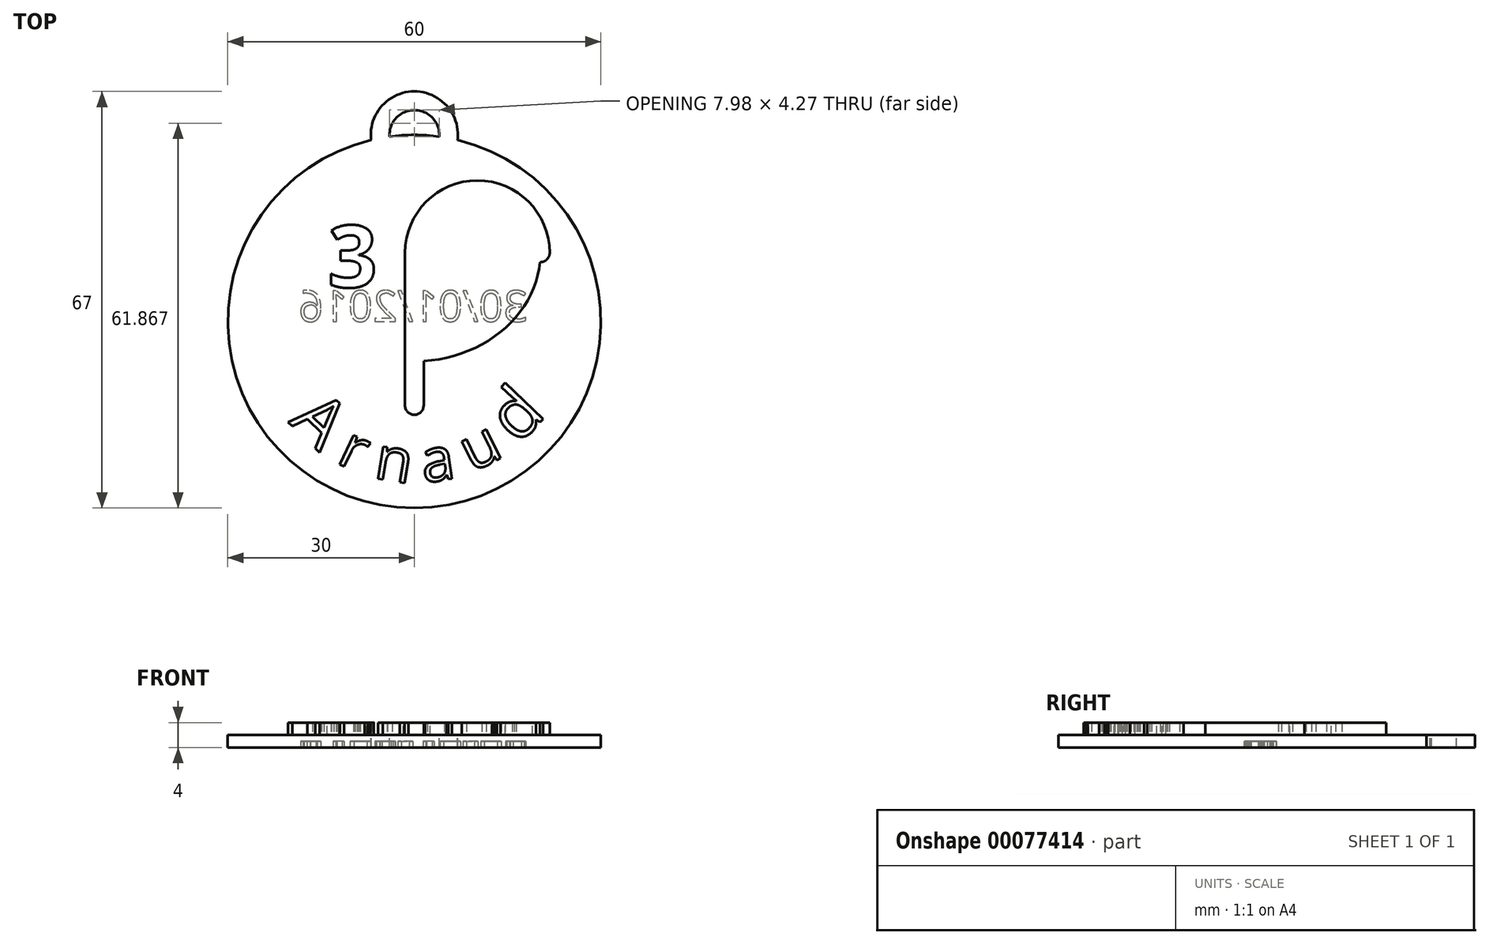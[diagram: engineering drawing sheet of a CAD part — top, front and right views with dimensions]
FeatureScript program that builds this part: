
annotation { "Feature Type Name" : "Feature", "Feature Type Description" : "" }
export const myFeature = defineFeature(function(context is Context, id is Id, definition is map)
    precondition{}
    {
        {
            var Q0;
            Q0=qCreatedBy(makeId("Top.planeOp"),FACE);
            var sketch = newSketch(context, id + "F0", { "sketchPlane" : qUnion([Q0])});
            skCircle(sketch, "E0", {"center": v(0, 0) * mm, "radius": 30 * mm});
            skSolve(sketch);
        }
        {
            var Q0;
            Q0=qSketchRegion(id+"F0",true);
            extrude(context, id + "F1", {"entities" : qUnion([Q0]), "oppositeDirection" : true, "depth" : 2 * mm});
        }
        {
            var Q0;
            Q0=qCreatedBy(makeId("Top.planeOp"),FACE);
            var sketch = newSketch(context, id + "F2", { "sketchPlane" : qUnion([Q0])});
            skEllipticalArc(sketch, "E1", {});
            skLineSegment(sketch, "E2", {"start": v(0, 0) * mm, "end": v(0, 30) * mm, "construction": true});
            skLineSegment(sketch, "E3", {"start": v(0, 11.04) * mm, "end": v(0, -13.5) * mm});
            skArc(sketch, "E4", {"start": v(20.27, 11.04) * mm, "mid": v(10.13, 21.17) * mm, "end": v(0, 11.04) * mm});
            skLineSegment(sketch, "E5", {"start": v(0, 11.04) * mm, "end": v(-16.84, 20.76) * mm, "construction": true});
            skLineSegment(sketch, "E6", {"start": v(0, 11.04) * mm, "end": v(-20.27, 11.04) * mm, "construction": true});
            skArc(sketch, "E7.0.startCap", {"start": v(-1.5, 11.04) * mm, "mid": v(0, 12.54) * mm, "end": v(1.5, 11.04) * mm});
            skArc(sketch, "E7.0.endCap", {"start": v(1.5, -13.5) * mm, "mid": v(0, -15) * mm, "end": v(-1.5, -13.5) * mm});
            skLineSegment(sketch, "E7.0.left", {"start": v(1.5, 11.04) * mm, "end": v(1.5, -13.5) * mm});
            skLineSegment(sketch, "E7.0.right", {"start": v(-1.5, 11.04) * mm, "end": v(-1.5, -13.5) * mm});
            skArc(sketch, "E8.0.startCap", {"start": v(21.77, 11.04) * mm, "mid": v(20.27, 9.54) * mm, "end": v(18.77, 11.04) * mm});
            skArc(sketch, "E8.0.endCap", {"start": v(1.5, 11.04) * mm, "mid": v(0, 9.54) * mm, "end": v(-1.5, 11.04) * mm});
            skArc(sketch, "E8.0.left", {"start": v(18.77, 11.04) * mm, "mid": v(10.13, 19.67) * mm, "end": v(1.5, 11.04) * mm});
            skArc(sketch, "E8.0.right", {"start": v(21.77, 11.04) * mm, "mid": v(10.13, 22.67) * mm, "end": v(-1.5, 11.04) * mm});
            skArc(sketch, "E8.1.startCap", {"start": v(-18.02, 21.68) * mm, "mid": v(-15.91, 21.95) * mm, "end": v(-15.65, 19.84) * mm});
            skArc(sketch, "E8.1.endCap", {"start": v(18.77, 11.04) * mm, "mid": v(20.27, 12.54) * mm, "end": v(21.77, 11.04) * mm});
            skFitSpline(sketch, "E8.1.left", {"points": [v(18.7, 9.5) * mm, v(18.8, 11.04) * mm, v(18.7, 12.6) * mm, v(18.36, 14.63) * mm, v(17.66, 16.6) * mm, v(16.63, 18.49) * mm, v(15.37, 20.3) * mm, v(13.44, 22.32) * mm, v(11.07, 24) * mm, v(8.94, 25.1) * mm, v(6.7, 26.01) * mm, v(4.32, 26.63) * mm, v(1.87, 26.95) * mm, v(0, 27.03) * mm, v(-1.87, 26.95) * mm, v(-4.32, 26.63) * mm, v(-6.7, 26.01) * mm, v(-8.94, 25.1) * mm, v(-11.07, 24) * mm, v(-13.44, 22.32) * mm, v(-15.37, 20.3) * mm, v(-16.63, 18.49) * mm, v(-17.66, 16.6) * mm, v(-18.36, 14.63) * mm, v(-18.7, 12.6) * mm, v(-18.8, 11.04) * mm, v(-18.7, 9.5) * mm, v(-18.36, 7.46) * mm, v(-17.66, 5.48) * mm, v(-16.63, 3.6) * mm, v(-15.37, 1.8) * mm, v(-13.44, -0.24) * mm, v(-11.07, -1.92) * mm, v(-8.94, -3.02) * mm, v(-6.7, -3.93) * mm, v(-4.32, -4.55) * mm, v(-1.87, -4.86) * mm, v(0, -4.94) * mm, v(1.87, -4.86) * mm, v(4.32, -4.55) * mm, v(6.7, -3.93) * mm, v(8.94, -3.02) * mm, v(11.07, -1.92) * mm, v(13.44, -0.24) * mm, v(15.37, 1.8) * mm, v(16.63, 3.6) * mm, v(17.66, 5.48) * mm, v(18.36, 7.46) * mm, v(18.7, 9.5) * mm, v(18.8, 11.04) * mm, v(18.7, 12.6) * mm]});
            skFitSpline(sketch, "E8.1.right", {"points": [v(21.7, 9.15) * mm, v(21.8, 11.04) * mm, v(21.7, 12.93) * mm, v(21.27, 15.42) * mm, v(20.42, 17.81) * mm, v(19.18, 20.07) * mm, v(17.69, 22.22) * mm, v(15.4, 24.61) * mm, v(12.65, 26.56) * mm, v(10.2, 27.83) * mm, v(7.62, 28.88) * mm, v(4.92, 29.58) * mm, v(2.12, 29.94) * mm, v(0, 30.03) * mm, v(-2.12, 29.94) * mm, v(-4.92, 29.58) * mm, v(-7.62, 28.88) * mm, v(-10.2, 27.83) * mm, v(-12.65, 26.56) * mm, v(-15.4, 24.61) * mm, v(-17.69, 22.22) * mm, v(-19.18, 20.07) * mm, v(-20.42, 17.81) * mm, v(-21.27, 15.42) * mm, v(-21.7, 12.93) * mm, v(-21.8, 11.04) * mm, v(-21.7, 9.15) * mm, v(-21.27, 6.67) * mm, v(-20.42, 4.27) * mm, v(-19.18, 2) * mm, v(-17.69, -0.14) * mm, v(-15.4, -2.53) * mm, v(-12.65, -4.48) * mm, v(-10.2, -5.75) * mm, v(-7.62, -6.8) * mm, v(-4.92, -7.5) * mm, v(-2.12, -7.86) * mm, v(0, -7.95) * mm, v(2.12, -7.86) * mm, v(4.92, -7.5) * mm, v(7.62, -6.8) * mm, v(10.2, -5.75) * mm, v(12.65, -4.48) * mm, v(15.4, -2.53) * mm, v(17.69, -0.14) * mm, v(19.18, 2) * mm, v(20.42, 4.27) * mm, v(21.27, 6.67) * mm, v(21.7, 9.15) * mm, v(21.8, 11.04) * mm, v(21.7, 12.93) * mm]});
            const initialGuessF2  = {"E1": [0, 0.011041626236194823, 1, 0, 0.020266667008310185, 0.017458373763805178, 2.5511335140588507, 0]};
            skSetInitialGuess(sketch, initialGuessF2);
            skSolve(sketch);
        }
        {
            var Q0;
            {var subQ0=sQuery(id+"F2.wireOp",EDGE,"E8.1.startCap");Q0=makeQuery(id+"F2.imprint","IMPRINT",FACE,{"disambiguationData":[TD([[makeQuery(id+"F2.imprint","IMPRINT",EDGE,{"derivedFrom":subQ0}),-1.0]])]});}
            var Q1;
            {var subQ0=sQuery(id+"F2.wireOp",EDGE,"E7.0.right");var subQ1=sQuery(id+"F2.wireOp",EDGE,"E1");var subQ2=makeQuery(id+"F2.imprint","INTERSECT",VERTEX,{"derivedFrom":[subQ1,subQ0]});Q1=makeQuery(id+"F2.imprint","IMPRINT",FACE,{"disambiguationData":[TD([[makeQuery(id+"F2.imprint","IMPRINT",EDGE,{"disambiguationData":[TD([[subQ2,-1.0]])],"derivedFrom":subQ1}),1.0]])]});}
            var Q2;
            {var subQ0=sQuery(id+"F2.wireOp",EDGE,"E3");var subQ1=sQuery(id+"F2.wireOp",EDGE,"E1");var subQ2=makeQuery(id+"F2.imprint","INTERSECT",VERTEX,{"derivedFrom":[subQ1,subQ0]});Q2=makeQuery(id+"F2.imprint","IMPRINT",FACE,{"disambiguationData":[TD([[makeQuery(id+"F2.imprint","IMPRINT",EDGE,{"disambiguationData":[TD([[subQ2,-1.0]])],"derivedFrom":subQ1}),1.0]])]});}
            var Q3;
            {var subQ0=sQuery(id+"F2.wireOp",EDGE,"E7.0.right");var subQ1=sQuery(id+"F2.wireOp",EDGE,"E1");var subQ2=makeQuery(id+"F2.imprint","INTERSECT",VERTEX,{"derivedFrom":[subQ1,subQ0]});Q3=makeQuery(id+"F2.imprint","IMPRINT",FACE,{"disambiguationData":[TD([[makeQuery(id+"F2.imprint","IMPRINT",EDGE,{"disambiguationData":[TD([[subQ2,-1.0]])],"derivedFrom":subQ1}),-1.0]])]});}
            var Q4;
            {var subQ0=sQuery(id+"F2.wireOp",EDGE,"E3");var subQ1=sQuery(id+"F2.wireOp",EDGE,"E1");var subQ2=makeQuery(id+"F2.imprint","INTERSECT",VERTEX,{"derivedFrom":[subQ1,subQ0]});Q4=makeQuery(id+"F2.imprint","IMPRINT",FACE,{"disambiguationData":[TD([[makeQuery(id+"F2.imprint","IMPRINT",EDGE,{"disambiguationData":[TD([[subQ2,-1.0]])],"derivedFrom":subQ1}),-1.0]])]});}
            var Q5;
            {var subQ0=sQuery(id+"F2.wireOp",EDGE,"E7.0.left");var subQ1=sQuery(id+"F2.wireOp",EDGE,"E1");var subQ2=makeQuery(id+"F2.imprint","INTERSECT",VERTEX,{"derivedFrom":[subQ1,subQ0]});Q5=makeQuery(id+"F2.imprint","IMPRINT",FACE,{"disambiguationData":[TD([[makeQuery(id+"F2.imprint","IMPRINT",EDGE,{"disambiguationData":[TD([[subQ2,-1.0]])],"derivedFrom":subQ1}),-1.0]])]});}
            var Q6;
            {var subQ0=sQuery(id+"F2.wireOp",EDGE,"E7.0.left");var subQ1=sQuery(id+"F2.wireOp",EDGE,"E1");var subQ2=makeQuery(id+"F2.imprint","INTERSECT",VERTEX,{"derivedFrom":[subQ1,subQ0]});Q6=makeQuery(id+"F2.imprint","IMPRINT",FACE,{"disambiguationData":[TD([[makeQuery(id+"F2.imprint","IMPRINT",EDGE,{"disambiguationData":[TD([[subQ2,-1.0]])],"derivedFrom":subQ1}),1.0]])]});}
            var Q7;
            {var subQ0=sQuery(id+"F2.wireOp",EDGE,"E4");var subQ1=sQuery(id+"F2.wireOp",EDGE,"E1");var subQ2=makeQuery(id+"F2.imprint","INTERSECT",VERTEX,{"derivedFrom":[subQ1,subQ0]});Q7=makeQuery(id+"F2.imprint","IMPRINT",FACE,{"disambiguationData":[TD([[makeQuery(id+"F2.imprint","IMPRINT",EDGE,{"disambiguationData":[TD([[subQ2,1.0]])],"derivedFrom":subQ1}),-1.0]])]});}
            var Q8;
            {var subQ0=sQuery(id+"F2.wireOp",EDGE,"E4");var subQ1=sQuery(id+"F2.wireOp",EDGE,"E1");var subQ2=makeQuery(id+"F2.imprint","INTERSECT",VERTEX,{"derivedFrom":[subQ1,subQ0]});Q8=makeQuery(id+"F2.imprint","IMPRINT",FACE,{"disambiguationData":[TD([[makeQuery(id+"F2.imprint","IMPRINT",EDGE,{"disambiguationData":[TD([[subQ2,1.0]])],"derivedFrom":subQ1}),1.0]])]});}
            var Q9;
            {var subQ5=sQuery(id+"F2.wireOp",EDGE,"E8.0.left");Q9=makeQuery(id+"F2.imprint","IMPRINT",FACE,{"disambiguationData":[TD([[makeQuery(id+"F2.imprint","IMPRINT",EDGE,{"derivedFrom":subQ5}),-1.0]])]});}
            var Q10;
            {var subQ5=sQuery(id+"F2.wireOp",EDGE,"E8.0.right");Q10=makeQuery(id+"F2.imprint","IMPRINT",FACE,{"disambiguationData":[TD([[makeQuery(id+"F2.imprint","IMPRINT",EDGE,{"derivedFrom":subQ5}),1.0]])]});}
            var Q11;
            {var subQ0=sQuery(id+"F2.wireOp",EDGE,"E4");var subQ1=sQuery(id+"F2.wireOp",EDGE,"E3");var subQ2=makeQuery(id+"F2.imprint","INTERSECT",VERTEX,{"derivedFrom":[subQ1,subQ0]});Q11=makeQuery(id+"F2.imprint","IMPRINT",FACE,{"disambiguationData":[TD([[makeQuery(id+"F2.imprint","IMPRINT",EDGE,{"disambiguationData":[TD([[subQ2,-1.0]])],"derivedFrom":subQ1}),-1.0]])]});}
            var Q12;
            {var subQ0=sQuery(id+"F2.wireOp",EDGE,"E4");var subQ1=sQuery(id+"F2.wireOp",EDGE,"E3");var subQ2=makeQuery(id+"F2.imprint","INTERSECT",VERTEX,{"derivedFrom":[subQ1,subQ0]});Q12=makeQuery(id+"F2.imprint","IMPRINT",FACE,{"disambiguationData":[TD([[makeQuery(id+"F2.imprint","IMPRINT",EDGE,{"disambiguationData":[TD([[subQ2,-1.0]])],"derivedFrom":subQ1}),1.0]])]});}
            var Q13;
            {var subQ0=sQuery(id+"F2.wireOp",EDGE,"E8.0.endCap");var subQ1=sQuery(id+"F2.wireOp",EDGE,"E3");var subQ2=makeQuery(id+"F2.imprint","INTERSECT",VERTEX,{"derivedFrom":[subQ1,subQ0]});Q13=makeQuery(id+"F2.imprint","IMPRINT",FACE,{"disambiguationData":[TD([[makeQuery(id+"F2.imprint","IMPRINT",EDGE,{"disambiguationData":[TD([[subQ2,-1.0]])],"derivedFrom":subQ1}),-1.0]])]});}
            var Q14;
            {var subQ0=sQuery(id+"F2.wireOp",EDGE,"E8.0.endCap");var subQ1=sQuery(id+"F2.wireOp",EDGE,"E3");var subQ2=makeQuery(id+"F2.imprint","INTERSECT",VERTEX,{"derivedFrom":[subQ1,subQ0]});Q14=makeQuery(id+"F2.imprint","IMPRINT",FACE,{"disambiguationData":[TD([[makeQuery(id+"F2.imprint","IMPRINT",EDGE,{"disambiguationData":[TD([[subQ2,-1.0]])],"derivedFrom":subQ1}),1.0]])]});}
            var Q15;
            {var subQ1=sQuery(id+"F2.wireOp",EDGE,"E7.0.endCap");Q15=makeQuery(id+"F2.imprint","IMPRINT",FACE,{"disambiguationData":[TD([[makeQuery(id+"F2.imprint","IMPRINT",EDGE,{"derivedFrom":subQ1}),-1.0]])]});}
            extrude(context, id + "F3", {"entities" : qUnion([Q0, Q1, Q2, Q3, Q4, Q5, Q6, Q7, Q8, Q9, Q10, Q11, Q12, Q13, Q14, Q15]), "operationType" : NewBodyOperationType.ADD, "depth" : 2 * mm});
        }
        {
            var Q0;
            Q0=qCreatedBy(makeId("Top.planeOp"),FACE);
            var sketch = newSketch(context, id + "F4", { "sketchPlane" : qUnion([Q0])});
            skText(sketch, "E9", { "text": "3", "fontName": "OpenSans-Bold.ttf"});
            skText(sketch, "E10", { "text": "D", "fontName": "OpenSans-Bold.ttf"});
            const initialGuessF4  = {"E9": [-0.0139, 0.0055, 1, 0, 0.01], "E10": [0.0055, 0.0055, 1, 0, 0.01]};
            skSetInitialGuess(sketch, initialGuessF4);
            skSolve(sketch);
        }
        {
            var Q0;
            Q0=qSketchRegion(id+"F4",true);
            extrude(context, id + "F5", {"entities" : qUnion([Q0]), "operationType" : NewBodyOperationType.ADD, "depth" : 2 * mm});
        }
        {
            var Q0;
            {var subQ8=sQuery(id+"F0.wireOp",EDGE,"E0");Q0=makeQuery(id+"F3.boolean.opBoolean","SPLIT",FACE,{"disambiguationData":[TD([makeQuery(id+"F1.opExtrude","SWEPT_FACE",FACE,{"disambiguationData":[OSD([subQ8])]})])],"derivedFrom":makeQuery(id+"F1.opExtrude","CAP_FACE",FACE,{"disambiguationData":[OSD([subQ8])],"isStart":true})});}
            var sketch = newSketch(context, id + "F6", { "sketchPlane" : qUnion([Q0])});
            skCircle(sketch, "E11.0", {"center": v(0, 0) * mm, "radius": 26 * mm, "construction": true});
            skText(sketch, "E12", { "text": "A", "fontName": "OpenSans-Regular.ttf"});
            skText(sketch, "E13", { "text": "r", "fontName": "OpenSans-Regular.ttf"});
            skText(sketch, "E14", { "text": "n", "fontName": "OpenSans-Regular.ttf"});
            skText(sketch, "E15", { "text": "a", "fontName": "OpenSans-Regular.ttf"});
            skText(sketch, "E16", { "text": "u", "fontName": "OpenSans-Regular.ttf"});
            skText(sketch, "E17", { "text": "d", "fontName": "OpenSans-Regular.ttf"});
            const initialGuessF6  = {"E12": [-0.02032, -0.01622, 0.72378, -0.69003, 0.008], "E13": [-0.01277, -0.02265, 0.90486, -0.42571, 0.007], "E14": [-0.00667, -0.02513, 0.98728, -0.15902, 0.007], "E15": [0.00149, -0.02596, 0.98934, 0.1456, 0.007], "E16": [0.00928, -0.02429, 0.8943, 0.44747, 0.007], "E17": [0.0167, -0.01993, 0.68945, 0.72433, 0.008]};
            skSetInitialGuess(sketch, initialGuessF6);
            skSolve(sketch);
        }
        {
            var Q0;
            Q0=qSketchRegion(id+"F6",true);
            extrude(context, id + "F7", {"entities" : qUnion([Q0]), "operationType" : NewBodyOperationType.ADD, "depth" : 2 * mm});
        }
        {
            var Q0;
            Q0=qCreatedBy(makeId("Top.planeOp"),FACE);
            var sketch = newSketch(context, id + "F8", { "sketchPlane" : qUnion([Q0])});
            skArc(sketch, "E18", {"start": v(5.48, 29.5) * mm, "mid": v(0, 35.5) * mm, "end": v(-5.48, 29.5) * mm});
            skArc(sketch, "E19.0.startCap", {"start": v(6.97, 29.36) * mm, "mid": v(5.34, 28) * mm, "end": v(3.98, 29.63) * mm});
            skArc(sketch, "E19.0.endCap", {"start": v(-3.98, 29.63) * mm, "mid": v(-5.34, 28) * mm, "end": v(-6.97, 29.36) * mm});
            skArc(sketch, "E19.0.left", {"start": v(3.98, 29.63) * mm, "mid": v(0, 34) * mm, "end": v(-3.98, 29.63) * mm});
            skArc(sketch, "E19.0.right", {"start": v(6.97, 29.36) * mm, "mid": v(0, 37) * mm, "end": v(-6.97, 29.36) * mm});
            skSolve(sketch);
        }
        {
            var Q0;
            Q0=qSketchRegion(id+"F8",true);
            extrude(context, id + "F9", {"entities" : qUnion([Q0]), "operationType" : NewBodyOperationType.ADD, "oppositeDirection" : true, "depth" : 2 * mm});
        }
        {
            var Q0;
            Q0=makeQuery(id+"F9.boolean.opBoolean","MERGE",FACE,{"derivedFrom":[makeQuery(id+"F1.opExtrude","CAP_FACE",FACE,{"disambiguationData":[OSD([sQuery(id+"F0.wireOp",EDGE,"E0")])],"isStart":false}),makeQuery(id+"F9.opExtrude","CAP_FACE",FACE,{"disambiguationData":[OSD([sQuery(id+"F8.wireOp",EDGE,"E19.0.startCap"),sQuery(id+"F8.wireOp",EDGE,"E19.0.endCap"),sQuery(id+"F8.wireOp",EDGE,"E19.0.left"),sQuery(id+"F8.wireOp",EDGE,"E19.0.right")])],"isStart":false})]});
            var sketch = newSketch(context, id + "F10", { "sketchPlane" : qUnion([Q0])});
            skText(sketch, "E20", { "text": "30/01/2016", "fontName": "OpenSans-Regular.ttf"});
            const initialGuessF10  = {"E20": [0.01826, 0, -1, 0, 0.005]};
            skSetInitialGuess(sketch, initialGuessF10);
            skSolve(sketch);
        }
        {
            var Q0;
            Q0=qSketchRegion(id+"F10",true);
            extrude(context, id + "F11", {"entities" : qUnion([Q0]), "operationType" : NewBodyOperationType.REMOVE, "oppositeDirection" : true, "depth" : 1 * mm});
        }
    });
